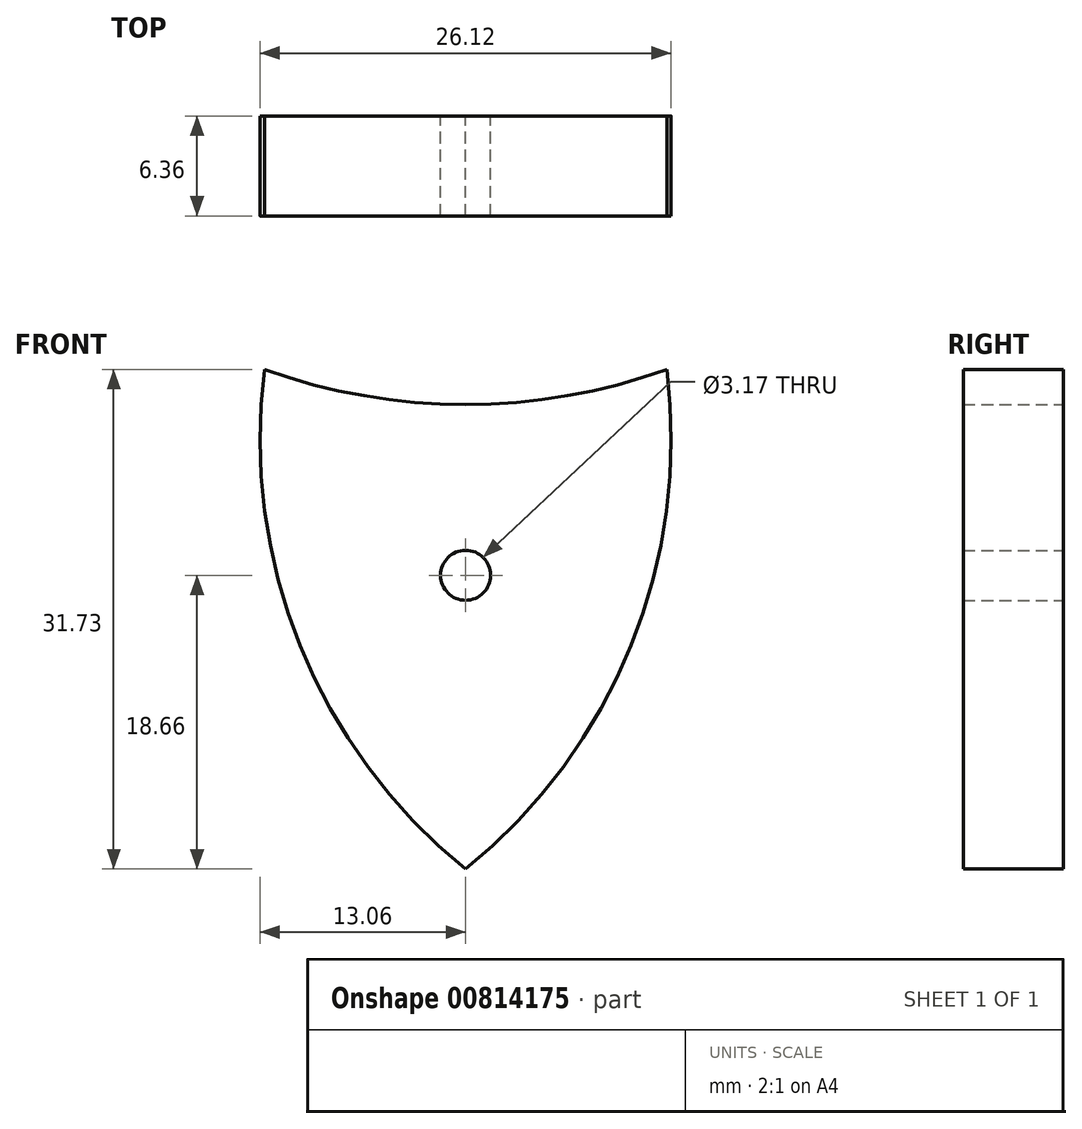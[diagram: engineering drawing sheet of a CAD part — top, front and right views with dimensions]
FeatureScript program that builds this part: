
annotation { "Feature Type Name" : "Feature", "Feature Type Description" : "" }
export const myFeature = defineFeature(function(context is Context, id is Id, definition is map)
    precondition{}
    {
        {
            var Q0;
            Q0=qCreatedBy(makeId("Front.planeOp"),FACE);
            var sketch = newSketch(context, id + "F0", { "sketchPlane" : qUnion([Q0])});
            skCircle(sketch, "E0", {"center": v(0, 0) * mm, "radius": 9.53 * mm});
            skArc(sketch, "E1", {"start": v(-12.78, 13.07) * mm, "mid": v(-10.51, -4.46) * mm, "end": v(0, -18.66) * mm});
            skArc(sketch, "E2.MirrorCS", {"start": v(12.78, 13.07) * mm, "mid": v(10.51, -4.46) * mm, "end": v(0, -18.66) * mm});
            skArc(sketch, "E3", {"start": v(-12.78, 13.07) * mm, "mid": v(0, 10.85) * mm, "end": v(12.78, 13.07) * mm});
            skCircle(sketch, "E4", {"center": v(0, 0) * mm, "radius": 1.59 * mm});
            skSolve(sketch);
        }
        {
            var Q0;
            Q0=makeQuery(id+"F0.imprint","IMPRINT",FACE,{"disambiguationData":[TD([[makeQuery(id+"F0.imprint","IMPRINT",EDGE,{"derivedFrom":sQuery(id+"F0.wireOp",EDGE,"E0")}),-1.0]])]});
            var Q1;
            Q1=makeQuery(id+"F0.imprint","IMPRINT",FACE,{"disambiguationData":[TD([[makeQuery(id+"F0.imprint","IMPRINT",EDGE,{"derivedFrom":sQuery(id+"F0.wireOp",EDGE,"E0")}),1.0]])]});
            extrude(context, id + "F1", {"entities" : qUnion([Q0, Q1]), "endBound" : BoundingType.SYMMETRIC, "depth" : 6.35 * mm, "offsetDistance" : 25 * mm});
        }
    });
